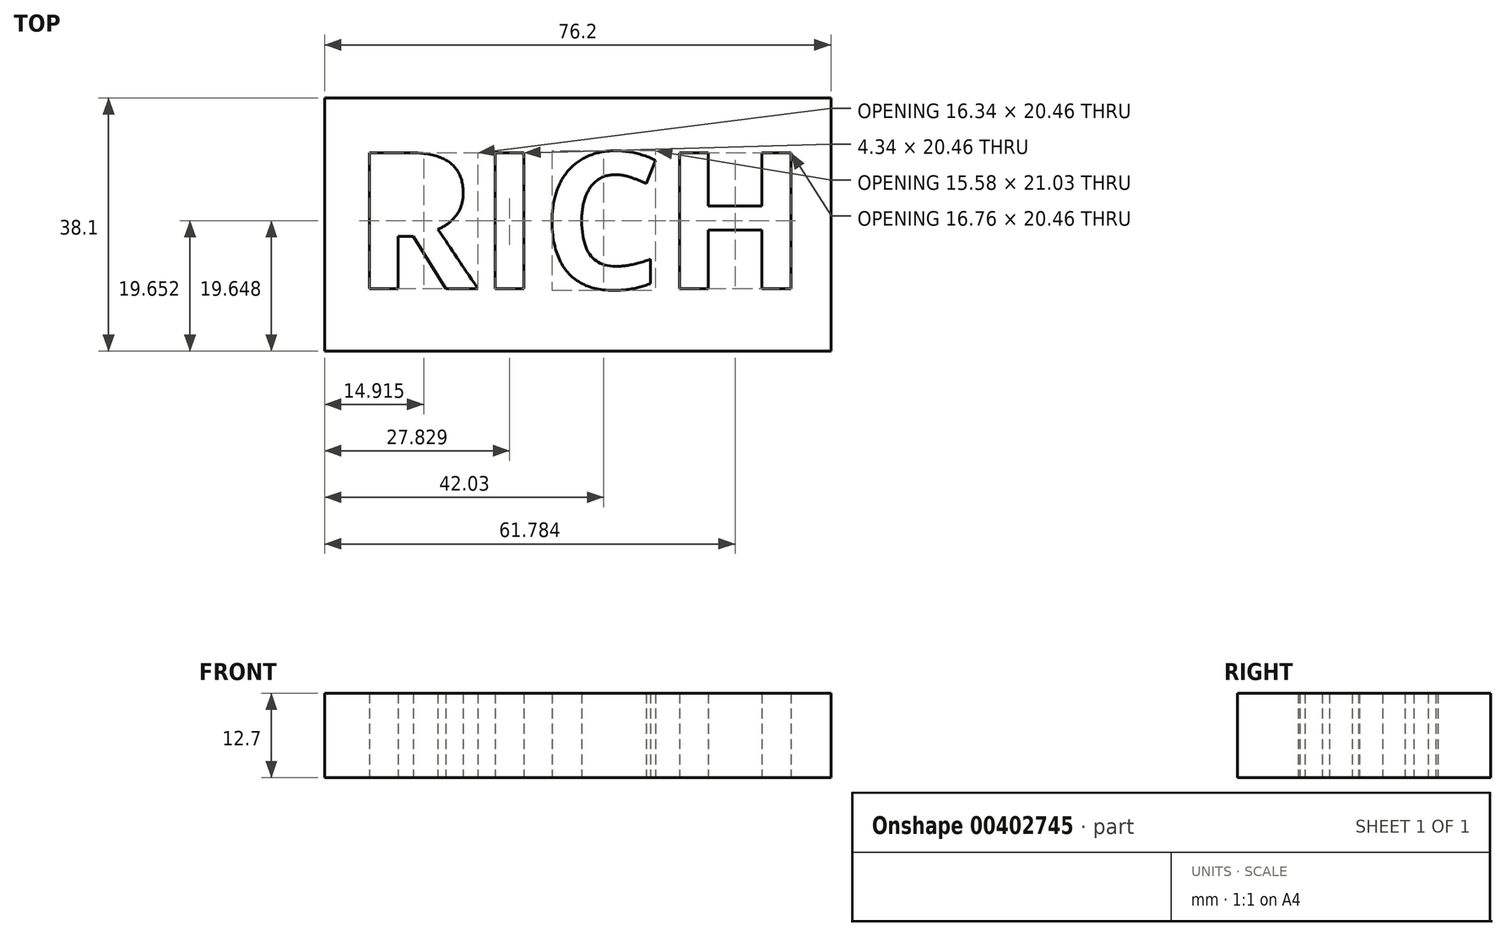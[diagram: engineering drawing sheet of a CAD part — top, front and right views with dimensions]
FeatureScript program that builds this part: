
annotation { "Feature Type Name" : "Feature", "Feature Type Description" : "" }
export const myFeature = defineFeature(function(context is Context, id is Id, definition is map)
    precondition{}
    {
        {
            var Q0;
            Q0=qCreatedBy(makeId("Top.planeOp"),FACE);
            var sketch = newSketch(context, id + "F0", { "sketchPlane" : qUnion([Q0])});
            skLineSegment(sketch, "E0.bottom", {"start": v(-38.1, 19.05) * mm, "end": v(38.1, 19.05) * mm});
            skLineSegment(sketch, "E0.top", {"start": v(-38.1, -19.05) * mm, "end": v(38.1, -19.05) * mm});
            skLineSegment(sketch, "E0.left", {"start": v(-38.1, 19.05) * mm, "end": v(-38.1, -19.05) * mm});
            skLineSegment(sketch, "E0.right", {"start": v(38.1, 19.05) * mm, "end": v(38.1, -19.05) * mm});
            skPoint(sketch, "E0.middle", {"position": v(0, 0) * mm});
            skText(sketch, "E1", { "text": "RICH", "fontName": "OpenSans-Bold.ttf"});
            const initialGuessF0  = {"E1": [-0.03393, -0.00963, 1, 0, 0.02063]};
            skSetInitialGuess(sketch, initialGuessF0);
            skSolve(sketch);
        }
        {
            var Q0;
            Q0 = qSketchRegion(id + "F0", true);
            extrude(context, id + "F1", {"entities" : qUnion([Q0]), "depth" : 12.7 * mm});
        }
    });
